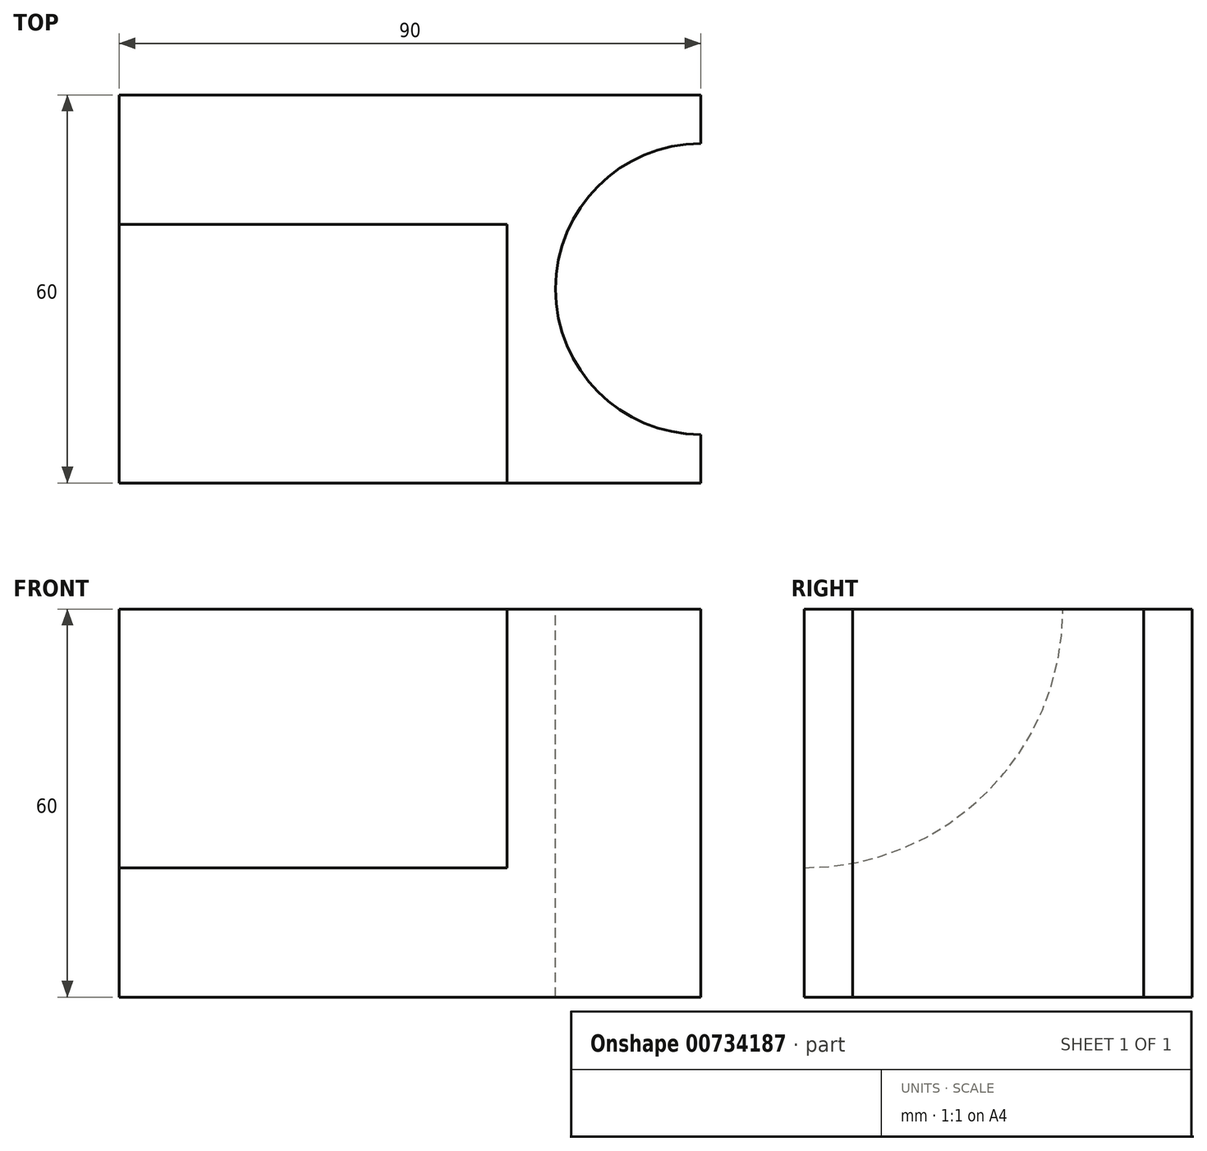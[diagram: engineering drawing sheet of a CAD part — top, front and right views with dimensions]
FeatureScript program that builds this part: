
annotation { "Feature Type Name" : "Feature", "Feature Type Description" : "" }
export const myFeature = defineFeature(function(context is Context, id is Id, definition is map)
    precondition{}
    {
        {
            var Q0;
            Q0=qCreatedBy(makeId("Top.planeOp"),FACE);
            var sketch = newSketch(context, id + "F0", { "sketchPlane" : qUnion([Q0])});
            skLineSegment(sketch, "E0", {"start": v(0, 0) * mm, "end": v(90, 0) * mm});
            skLineSegment(sketch, "E1", {"start": v(90, 0) * mm, "end": v(90, -60) * mm});
            skLineSegment(sketch, "E2", {"start": v(90, -60) * mm, "end": v(0, -60) * mm});
            skLineSegment(sketch, "E3", {"start": v(0, -60) * mm, "end": v(0, 0) * mm});
            skSolve(sketch);
        }
        {
            var Q0;
            Q0=makeQuery(id+"F0.imprint","IMPRINT",FACE,{"disambiguationData":[TD([[makeQuery(id+"F0.imprint","IMPRINT",EDGE,{"derivedFrom":sQuery(id+"F0.wireOp",EDGE,"E0")}),-1.0]])]});
            extrude(context, id + "F1", {"entities" : qUnion([Q0]), "depth" : 60 * mm, "offsetDistance" : 25 * mm});
        }
        {
            var Q0;
            Q0=makeQuery(id+"F1.opExtrude","CAP_FACE",FACE,{"disambiguationData":[OSD([sQuery(id+"F0.wireOp",EDGE,"E0"),sQuery(id+"F0.wireOp",EDGE,"E1"),sQuery(id+"F0.wireOp",EDGE,"E2"),sQuery(id+"F0.wireOp",EDGE,"E3")])],"isStart":false});
            var sketch = newSketch(context, id + "F2", { "sketchPlane" : qUnion([Q0])});
            skArc(sketch, "E4", {"start": v(90, -7.5) * mm, "mid": v(67.5, -30) * mm, "end": v(90, -52.5) * mm});
            skSolve(sketch);
        }
        {
            var Q0;
            {var subQ0=sQuery(id+"F2.wireOp",EDGE,"E4");Q0=makeQuery(id+"F2.imprint","IMPRINT",FACE,{"disambiguationData":[TD([[makeQuery(id+"F2.imprint","IMPRINT",EDGE,{"derivedFrom":subQ0}),1.0]])]});}
            var Q1;
            Q1=makeQuery(id+"F1.opExtrude","CAP_FACE",FACE,{"disambiguationData":[OSD([sQuery(id+"F0.wireOp",EDGE,"E0"),sQuery(id+"F0.wireOp",EDGE,"E1"),sQuery(id+"F0.wireOp",EDGE,"E2"),sQuery(id+"F0.wireOp",EDGE,"E3")])],"isStart":true});
            extrude(context, id + "F3", {"entities" : qUnion([Q0]), "operationType" : NewBodyOperationType.REMOVE, "endBound" : BoundingType.UP_TO_SURFACE, "oppositeDirection" : true, "depth" : 25 * mm, "endBoundEntityFace" : qUnion([Q1]), "offsetDistance" : 25 * mm});
        }
        {
            var Q0;
            Q0=makeQuery(id+"F1.opExtrude","SWEPT_FACE",FACE,{"disambiguationData":[OSD([sQuery(id+"F0.wireOp",EDGE,"E3")])]});
            var sketch = newSketch(context, id + "F4", { "sketchPlane" : qUnion([Q0])});
            skArc(sketch, "E5", {"start": v(20, 60) * mm, "mid": v(31.72, 31.72) * mm, "end": v(60, 20) * mm});
            skSolve(sketch);
        }
        {
            var Q0;
            Q0=makeQuery(id+"F1.opExtrude","SWEPT_FACE",FACE,{"disambiguationData":[OSD([sQuery(id+"F0.wireOp",EDGE,"E2")])]});
            var sketch = newSketch(context, id + "F5", { "sketchPlane" : qUnion([Q0])});
            skLineSegment(sketch, "E6", {"start": v(0, 60) * mm, "end": v(0, 100) * mm});
            skLineSegment(sketch, "E7", {"start": v(0, 100) * mm, "end": v(60, 100) * mm});
            skLineSegment(sketch, "E8", {"start": v(60, 100) * mm, "end": v(60, 60) * mm});
            skSolve(sketch);
        }
        {
            var Q0;
            {var subQ0=sQuery(id+"F5.wireOp",EDGE,"E6");Q0=makeQuery(id+"F5.imprint","IMPRINT",FACE,{"disambiguationData":[TD([[makeQuery(id+"F5.imprint","IMPRINT",EDGE,{"derivedFrom":subQ0}),-1.0]])]});}
            var Q1;
            Q1=makeQuery(id+"F1.opExtrude","CAP_EDGE",EDGE,{"disambiguationData":[OSD([sQuery(id+"F0.wireOp",EDGE,"E2")])],"isStart":false});
            revolve(context, id + "F6", {"operationType" : NewBodyOperationType.REMOVE, "surfaceOperationType" : NewSurfaceOperationType.NEW, "entities" : qUnion([Q0]), "axis" : qUnion([Q1]), "revolveType" : RevolveType.FULL, "oppositeDirection" : true});
        }
    });
